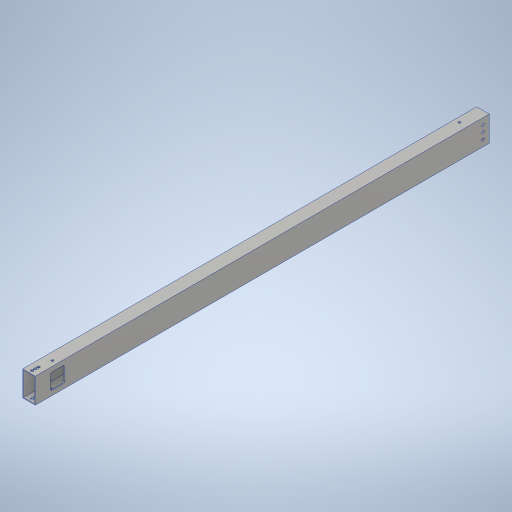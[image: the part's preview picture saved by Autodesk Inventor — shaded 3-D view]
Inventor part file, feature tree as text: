
AUTODESK INVENTOR PART (.ipt)
format: ipt  version: 2023.4 (Build 274418000, 418)  size: 332,288 bytes
history: native  units: in
note: dims shown in document units (in); Inventor stores cm internally (conversion verified against a paired STEP export)
features: sketch x6, hole x4, extrude x3, fillet x1
ambient origin geometry x8: Origin, YZ Plane, XZ Plane, XY Plane, X Axis, Y Axis, Z Axis, Center Point
bodies: Solid1 (feature_tree)
feature tree (14):
  extrude  "Extrusion1"  Depth=0.25in
  hole  "Hole1"  [1 undecoded]
  hole  "Hole2"  [1 undecoded]
  hole  "Hole3"  [1 undecoded]
  hole  "Hole4"  [1 undecoded]
  extrude  "Extrusion2"  Depth=0.125in
  extrude  "Extrusion3"  Depth=0.125in
  fillet  "Fillet1"  Radius=0.391in
  sketch  "Sketch2"  dims[d4=0.0in d5=0.25in]
  sketch  "Sketch3"  dims[d6=0.25in d7=0.25in]
  sketch  "Sketch4"  dims[d8=0.201in d9=0.38in d10=0.385in d11=0.25in d12=0.5635in d13=1.0in d14=0.8108in d15=0.5in]
  sketch  "Sketch5"  dims[d16=0.5in d17=0.5in]
  sketch  "Sketch6"  dims[d18=0.201in d19=0.75in d20=0.385in d21=0.25in d22=0.5635in d23=1.0in d24=0.8108in d26=1.0in]
  sketch  "Sketch7"  dims[d27=0.175in d28=0.75in d29=0.385in d30=0.25in d31=0.5635in d32=1.0in d33=0.8108in d34=0.391in d35=1.75in d36=0.391in d37=0.175in d38=0.75in d39=0.375in d40=0.25in d41=0.5635in d42=1.0in d43=0.8108in d44=1.2in d45=1.1in d47=1.25in d48=0.0625in d49=0.0in d50=1.2in d51=1.25in d52=1.1in d53=0.0625in d54=0.0in d55=0.125in]
note: 4 required parameter values undecoded (feature->parameter linkage not recoverable at this tier; creation-order binding heuristic only, values carry confidence <= 0.55)
